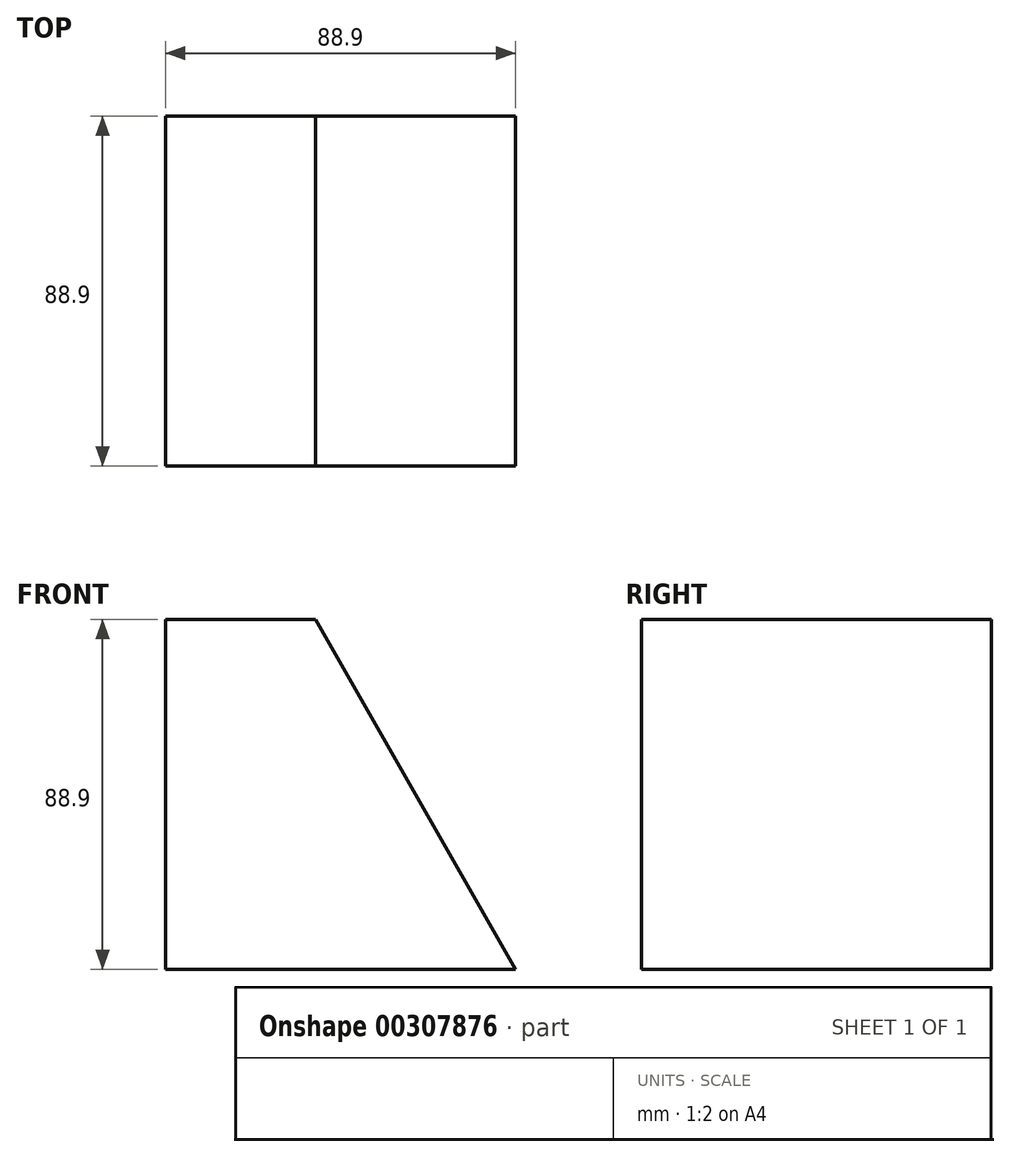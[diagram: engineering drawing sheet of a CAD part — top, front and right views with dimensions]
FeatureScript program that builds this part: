
annotation { "Feature Type Name" : "Feature", "Feature Type Description" : "" }
export const myFeature = defineFeature(function(context is Context, id is Id, definition is map)
    precondition{}
    {
        {
            var Q0;
            Q0=qCreatedBy(makeId("Front.planeOp"),FACE);
            var sketch = newSketch(context, id + "F0", { "sketchPlane" : qUnion([Q0])});
            skLineSegment(sketch, "E0", {"start": v(-5.63, 36.4) * mm, "end": v(-43.73, 36.4) * mm});
            skLineSegment(sketch, "E1", {"start": v(-43.73, 36.4) * mm, "end": v(-43.73, -52.5) * mm});
            skLineSegment(sketch, "E2", {"start": v(-43.73, -52.5) * mm, "end": v(45.17, -52.5) * mm});
            skLineSegment(sketch, "E3", {"start": v(-5.63, 36.4) * mm, "end": v(45.17, -52.5) * mm});
            skSolve(sketch);
        }
        {
            var Q0;
            Q0=makeQuery(id+"F0.imprint","IMPRINT",FACE,{"disambiguationData":[TD([[makeQuery(id+"F0.imprint","IMPRINT",EDGE,{"derivedFrom":sQuery(id+"F0.wireOp",EDGE,"E0")}),1.0]])]});
            extrude(context, id + "F1", {"entities" : qUnion([Q0]), "depth" : 88.9 * mm});
        }
    });
